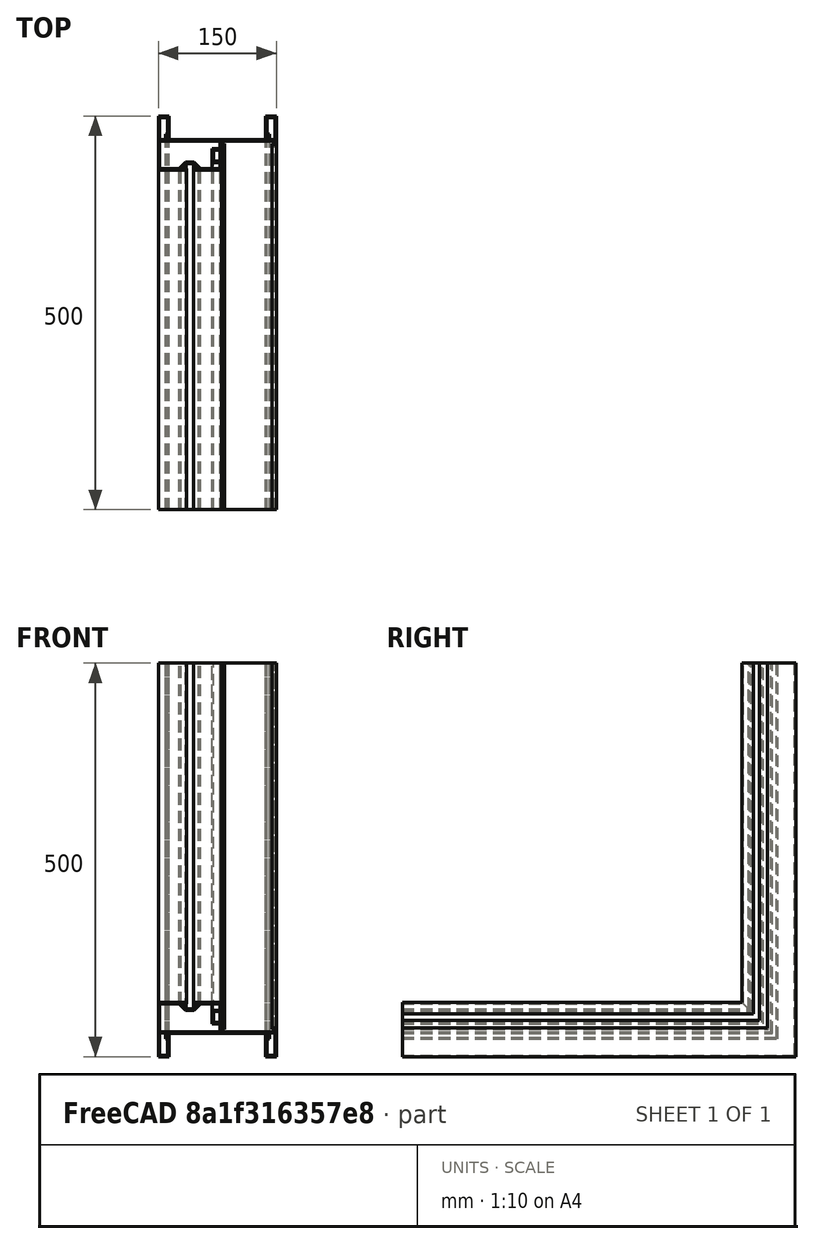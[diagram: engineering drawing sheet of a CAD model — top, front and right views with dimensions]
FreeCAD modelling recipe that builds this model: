
FCSTD DOCUMENT  (FreeCAD 0.21R33694 (Git))
Label: Profile_stripped
License: All rights reserved
LicenseURL: http://en.wikipedia.org/wiki/All_rights_reserved
objects: Part::Feature×5, Part::FeaturePython×4, Part::Face×1, Part::Extrusion×1, Fem::FemSolverObjectPython×1, App::MaterialObjectPython×1, PartDesign::Plane×1, Fem::ConstraintFixed×1, Fem::ConstraintForce×1, Part::MultiFuse×1, Fem::FemMeshObjectPython×1, Fem::FemAnalysis×1
note: 13 computed .brp shape members not serialized (recipe doc carries the construction recipe); baked Part::Feature solids carry a one-line shape summary decoded from their .brp

FEATURE [Part::Feature] Shape
  shape: bbox 150 x 68.8 x 2e-07 mm, 0 faces, 0 solids (baked)
FEATURE [Part::Feature] Shape001
  shape: bbox 10.2 x 28.2 x 2e-07 mm, 0 faces, 0 solids (baked)
FEATURE [Part::Feature] Shape002
  shape: bbox 76.4 x 35.2 x 2e-07 mm, 0 faces, 0 solids (baked)
FEATURE [Part::Feature] Shape003
  shape: bbox 10.2 x 28.2 x 2e-07 mm, 0 faces, 0 solids (baked)
FEATURE [Part::Face] Face
  FaceMakerClass = Part::FaceMakerBullseye
  Sources = -> [Shape003,Shape002,Shape001,Shape]
FEATURE [Part::Extrusion] Extrude
  Base = -> Face
  Dir = (0,0,1)
  DirMode = 2
  FaceMakerClass = Part::FaceMakerBullseye
  LengthFwd = 500
  LengthRev = 0
  Placement = pos=(0,-68.8,0) rot=(0,0,1;0rad)
  Solid = false
  Symmetric = false
FEATURE [Fem::FemSolverObjectPython] SolverCcxTools  # FEM object (typed FeaturePython)
  AnalysisType = 0
  BeamShellResultOutput3D = false
  BucklingFactors = 1
  EigenmodeHighLimit = 1000000
  EigenmodeLowLimit = 0
  EigenmodesCount = 10
  GeometricalNonlinearity = 0
  IterationsControlParameterCutb = 0.25,0.5,0.75,0.85,,,1.5,
  IterationsControlParameterIter = 4,8,9,200,10,400,,200,,
  IterationsControlParameterTimeUse = false
  IterationsThermoMechMaximum = 2000
  IterationsUserDefinedIncrementations = false
  IterationsUserDefinedTimeStepLength = false
  MaterialNonlinearity = 0
  MatrixSolverType = 0
  SplitInputWriter = false
  ThermoMechSteadyState = true
  TimeEnd = 1
  TimeInitialStep = 0.01
FEATURE [App::MaterialObjectPython] MaterialSolid  # material (typed FeaturePython)
  Category = 0
  Material = AuthorAndLicense=CalculiX-Steel,CardName=CalculiX-Steel,Density=7900 kg/m^3,Description=Standard steel material for CalculiX sample calculations,+7 more (map truncated)
FEATURE [Part::Feature] Extrude001  label="ExtrudeCopy"
  Placement = pos=(0,-500,68.8) rot=(-1,0,0;1.5708rad)
  shape: bbox 150 x 500 x 68.8 mm, 64 faces (baked)
FEATURE [PartDesign::Plane] PartDesign__Plane002
  AttachmentOffset = pos=(0,0,0) rot=(-1,0,0;0.785398rad)
  Length = 259.59
  MapMode = 49
  Placement = pos=(0,0,2.274e-13) rot=(-1,0,0;0.785398rad)
  ResizeMode = 0
  Support = -> [Extrude001]
  Width = 838.26
FEATURE [Part::FeaturePython] Slice002  # WARN: FeaturePython — macro-defined, semantics opaque (R4)
  Base = -> Extrude001
  Mode = 1
  Tolerance = 0
  Tools = -> [PartDesign__Plane002]
FEATURE [Part::FeaturePython] Slice002_child0  label="Slice002.0"  # WARN: FeaturePython — macro-defined, semantics opaque (R4)
  Base = -> Slice002
  FilterType = 1
  Invert = false
  OverrideMaxVal = 0
  WindowFrom = 80
  WindowTo = 100
  items = 0
FEATURE [Fem::ConstraintFixed] ConstraintFixed
  NormalDirection = (-1,0,0)
  Normals = (13) [(-1,0,0),(-1,0,0),(-1,0,0),(-1,0,0),(-1,0,0),(-1,0,0),(-1,0,0),(-1,0,0),(-1,0,0),(-1,0,0),(-1,0,0),(-1,0,0),(-1,0,0)]
  Points = (13) [(0,0,2.27374e-13),(0,-166.667,68.8),(0,-166.667,45.8667),(0,-166.667,22.9333),(0,-166.667,2.27374e-13),(0,-333.333,68.8),(0,-333.333,45.8667),+6 more]
  References = -> [Slice002_child0]
  Scale = 18
FEATURE [Part::FeaturePython] Slice003  # WARN: FeaturePython — macro-defined, semantics opaque (R4)
  Base = -> Extrude
  Mode = 1
  Tolerance = 0
  Tools = -> [PartDesign__Plane002]
FEATURE [Part::FeaturePython] Slice003_child0  label="Slice003.0"  # WARN: FeaturePython — macro-defined, semantics opaque (R4)
  Base = -> Slice003
  FilterType = 1
  Invert = false
  OverrideMaxVal = 0
  WindowFrom = 80
  WindowTo = 100
  items = 0
FEATURE [Fem::ConstraintForce] ConstraintForce
  DirectionVector = (0,1,0)
  Force = 100
  NormalDirection = (0,-1,0)
  Points = (16) [(148.2,-31.8,500),(125.467,-31.8,500),(102.733,-31.8,500),(80,-31.8,500),(148.2,-31.8,343.933),(125.467,-31.8,343.933),(102.733,-31.8,343.933),+9 more]
  References = -> [Slice003_child0]
  Reversed = true
  Scale = 17
FEATURE [Part::MultiFuse] Fusion
  Refine = true
  Shapes = -> [Slice003_child0,Slice002_child0]
FEATURE [Fem::FemMeshObjectPython] FEMMeshGmsh  # FEM object (typed FeaturePython)
  Algorithm2D = 0
  Algorithm3D = 0
  CharacteristicLengthMax = 4
  CharacteristicLengthMin = 0
  CoherenceMesh = true
  ElementDimension = 3
  ElementOrder = 1
  GeometryTolerance = 0
  GroupsOfNodes = true
  HighOrderOptimize = 0
  MeshSizeFromCurvature = 12
  OptimizeNetgen = false
  OptimizeStd = true
  Part = -> Fusion
  RecombinationAlgorithm = 0
  Recombine3DAll = false
  RecombineAll = false
  SecondOrderLinear = false
FEATURE [Fem::FemAnalysis] Analysis
  Group = -> [SolverCcxTools,FEMMeshGmsh,ConstraintForce,ConstraintFixed,MaterialSolid]
